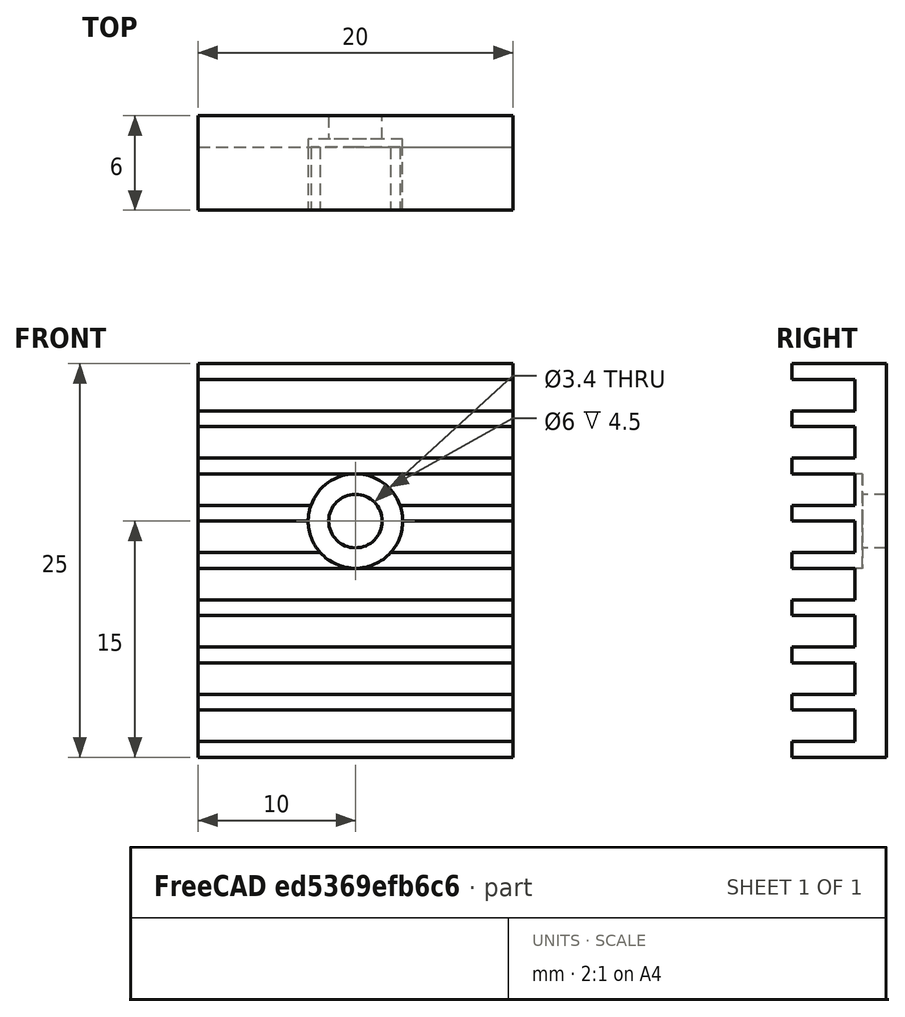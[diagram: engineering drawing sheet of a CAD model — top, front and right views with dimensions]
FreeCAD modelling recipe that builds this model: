
FCSTD DOCUMENT  (FreeCAD 0.19R24291 (Git))
Label: HVPS_Enclosure
License: All rights reserved
LicenseURL: http://en.wikipedia.org/wiki/All_rights_reserved
objects: TechDraw::DrawViewDimension×16, Sketcher::SketchObject×4, PartDesign::Pocket×3, TechDraw::DrawViewPart×3, PartDesign::Pad×1, PartDesign::LinearPattern×1, PartDesign::Body×1, TechDraw::DrawSVGTemplate×1, TechDraw::DrawPage×1
note: 14 computed .brp shape members not serialized (recipe doc carries the construction recipe); baked Part::Feature solids carry a one-line shape summary decoded from their .brp

FEATURE [Sketcher::SketchObject] Sketch
  FullyConstrained = true
  MapMode = 5
  Placement = pos=(0,0,0) rot=(1,0,0;1.5708rad)
  Support = -> [XZ_Plane002]
  sketch-geometry (4):
    g0: LineSegment StartX=-10 StartY=12.5 StartZ=0 EndX=10 EndY=12.5 EndZ=0
    g1: LineSegment StartX=10 StartY=12.5 StartZ=0 EndX=10 EndY=-12.5 EndZ=0
    g2: LineSegment StartX=10 StartY=-12.5 StartZ=0 EndX=-10 EndY=-12.5 EndZ=0
    g3: LineSegment StartX=-10 StartY=-12.5 StartZ=0 EndX=-10 EndY=12.5 EndZ=0
  constraints (10):
    c: Coincident(g0,g1)
    c: Coincident(g1,g2)
    c: Coincident(g2,g3)
    c: Coincident(g3,g0)
    c: Horizontal(g2)
    c: Vertical(g3)
    c: Symmetric(g0,g1,g-1)
    c: Symmetric(g0,g0,g-2)
    c: DistanceY(g3,g3) = 25
    c: DistanceX(g2,g2) = 20
FEATURE [PartDesign::Pad] Pad
  Direction = (1,1,1)
  Length = 6
  Length2 = 100
  Placement = pos=(0,0,0) rot=(1,0,0;1.5708rad)
  Profile = -> Sketch
  Type = 0
FEATURE [Sketcher::SketchObject] Sketch001
  ExternalGeometry = -> [Pad]
  FullyConstrained = true
  MapMode = 5
  Placement = pos=(0,-6,2.7e-15) rot=(1,0,0;1.5708rad)
  Support = -> [Pad]
  sketch-geometry (1):
    g0: Circle CenterX=0 CenterY=2.5 CenterZ=0 NormalX=0 NormalY=0 NormalZ=1 AngleXU=0 Radius=1.7
  constraints (3):
    c: PointOnObject(g0,g-2)
    c: Diameter(g0) = 3.4
    c: DistanceY(g0,g-3) = 10
FEATURE [PartDesign::Pocket] Pocket
  BaseFeature = -> Pad
  Length = 10
  Length2 = 100
  Placement = pos=(0,0,0) rot=(1,0,0;1.5708rad)
  Profile = -> Sketch001
  Type = 0
FEATURE [Sketcher::SketchObject] Sketch002
  ExternalGeometry = -> [Pocket]
  FullyConstrained = true
  MapMode = 5
  Placement = pos=(-10,0,0) rot=(0.707107,0,-0.707107;3.14159rad)
  Support = -> [Pocket]
  sketch-geometry (5):
    g0: LineSegment StartX=-11.5 StartY=6 StartZ=0 EndX=-9.5 EndY=6 EndZ=0
    g1: LineSegment StartX=-9.5 StartY=6 StartZ=0 EndX=-9.5 EndY=2 EndZ=0
    g2: LineSegment StartX=-9.5 StartY=2 StartZ=0 EndX=-11.5 EndY=2 EndZ=0
    g3: LineSegment StartX=-11.5 StartY=2 StartZ=0 EndX=-11.5 EndY=6 EndZ=0
    g4: LineSegment StartX=-9.5 StartY=6 StartZ=0 EndX=-8.5 EndY=6 EndZ=0
  constraints (15):
    c: Coincident(g0,g1)
    c: Coincident(g1,g2)
    c: Coincident(g2,g3)
    c: Coincident(g3,g0)
    c: Horizontal(g0)
    c: Horizontal(g2)
    c: Vertical(g1)
    c: Vertical(g3)
    c: PointOnObject(g0,g-3)
    c: DistanceX(g-3,g0) = 1
    c: DistanceY(g3,g3) = 4
    c: DistanceX(g2,g2) = 2
    c: Coincident(g4,g0)
    c: PointOnObject(g4,g-3)
    c: DistanceX(g4,g4) = 1
FEATURE [PartDesign::Pocket] Pocket001
  BaseFeature = -> Pocket
  Length = 25
  Length2 = 100
  Placement = pos=(0,0,0) rot=(1,0,0;1.5708rad)
  Profile = -> Sketch002
  Type = 0
FEATURE [PartDesign::LinearPattern] LinearPattern
  BaseFeature = -> Pocket001
  Direction = -> Z_Axis002
  Length = 21
  Occurrences = 8
  Originals = -> [Pocket001]
  Placement = pos=(0,0,0) rot=(1,0,0;1.5708rad)
  Reversed = true
FEATURE [Sketcher::SketchObject] Sketch003
  ExternalGeometry = -> [LinearPattern]
  FullyConstrained = true
  MapMode = 5
  Placement = pos=(0,-6,2.7e-15) rot=(1,0,0;1.5708rad)
  Support = -> [LinearPattern]
  sketch-geometry (1):
    g0: Circle CenterX=0 CenterY=2.5 CenterZ=0 NormalX=0 NormalY=0 NormalZ=1 AngleXU=0 Radius=3
  constraints (2):
    c: Coincident(g0,g-3)
    c: Diameter(g0) = 6
FEATURE [PartDesign::Pocket] Pocket002
  BaseFeature = -> LinearPattern
  Length = 4.5
  Length2 = 100
  Placement = pos=(0,0,0) rot=(1,0,0;1.5708rad)
  Profile = -> Sketch003
  Type = 0
FEATURE [PartDesign::Body] Body002  label="Heatsink"
  Group = -> [Sketch,Pad,Sketch001,Pocket,Sketch002,Pocket001,LinearPattern,Sketch003,Pocket002]
  Origin = -> Origin002
  Placement = pos=(0,100,0) rot=(0,0,1;0rad)
  Tip = -> Pocket002
FEATURE [TechDraw::DrawViewPart] View  label="front"
  CoarseView = false
  Direction = (0,-1,0)
  Focus = 100
  HardHidden = false
  IsoCount = 0
  IsoHidden = false
  IsoVisible = false
  LockPosition = false
  Perspective = false
  Rotation = 0
  Scale = 3
  ScaleType = 2
  SeamHidden = false
  SeamVisible = true
  SmoothHidden = false
  SmoothVisible = true
  Source = -> [Body002]
  X = 220.183
  XDirection = (1,0,0)
  Y = 124.936
FEATURE [TechDraw::DrawViewPart] View001  label="side"
  CoarseView = false
  Direction = (1,0,0)
  Focus = 100
  HardHidden = false
  IsoCount = 0
  IsoHidden = false
  IsoVisible = false
  LockPosition = false
  Perspective = false
  Rotation = 0
  Scale = 3
  ScaleType = 2
  SeamHidden = false
  SeamVisible = true
  SmoothHidden = false
  SmoothVisible = true
  Source = -> [Body002]
  X = 143.974
  XDirection = (0,1,0)
  Y = 125.785
FEATURE [TechDraw::DrawViewDimension] Dimension
  Arbitrary = false
  ArbitraryTolerances = false
  EqualTolerance = true
  FormatSpec = ⌀%.2f
  FormatSpecOverTolerance = %+.2f
  FormatSpecUnderTolerance = %+.2f
  Inverted = false
  LockPosition = false
  MeasureType = 1
  OverTolerance = 0
  References2D = -> [View]
  Rotation = 0
  ScaleType = 0
  TheoreticalExact = false
  Type = 5
  UnderTolerance = 0
  X = -40.1954
  Y = -0.362121
FEATURE [TechDraw::DrawViewDimension] Dimension001
  Arbitrary = false
  ArbitraryTolerances = false
  EqualTolerance = true
  FormatSpec = ⌀%.2f
  FormatSpecOverTolerance = %+.2f
  FormatSpecUnderTolerance = %+.2f
  Inverted = false
  LockPosition = false
  MeasureType = 1
  OverTolerance = 0
  References2D = -> [View]
  Rotation = 0
  ScaleType = 0
  TheoreticalExact = false
  Type = 5
  UnderTolerance = 0
  X = 38.4341
  Y = 1.73625
FEATURE [TechDraw::DrawViewDimension] Dimension002
  Arbitrary = false
  ArbitraryTolerances = false
  EqualTolerance = true
  FormatSpec = %.2f
  FormatSpecOverTolerance = %+.2f
  FormatSpecUnderTolerance = %+.2f
  Inverted = false
  LockPosition = false
  MeasureType = 1
  OverTolerance = 0
  References2D = -> [View]
  Rotation = 0
  ScaleType = 0
  TheoreticalExact = false
  Type = 2
  UnderTolerance = 0
  X = -51.2927
  Y = 0.724242
FEATURE [TechDraw::DrawViewDimension] Dimension003
  Arbitrary = false
  ArbitraryTolerances = false
  EqualTolerance = true
  FormatSpec = %.2f
  FormatSpecOverTolerance = %+.2f
  FormatSpecUnderTolerance = %+.2f
  Inverted = false
  LockPosition = false
  MeasureType = 1
  OverTolerance = 0
  References2D = -> [View]
  Rotation = 0
  ScaleType = 0
  TheoreticalExact = false
  Type = 1
  UnderTolerance = 0
  X = -0.289697
  Y = 52.8539
FEATURE [TechDraw::DrawViewDimension] Dimension004
  Arbitrary = false
  ArbitraryTolerances = false
  EqualTolerance = true
  FormatSpec = %.2f
  FormatSpecOverTolerance = %+.2f
  FormatSpecUnderTolerance = %+.2f
  Inverted = false
  LockPosition = false
  MeasureType = 1
  OverTolerance = 0
  References2D = -> [View]
  Rotation = 0
  ScaleType = 0
  TheoreticalExact = false
  Type = 2
  UnderTolerance = 0
  X = 39.7925
  Y = 49.9863
FEATURE [TechDraw::DrawViewDimension] Dimension005
  Arbitrary = false
  ArbitraryTolerances = false
  EqualTolerance = true
  FormatSpec = %.2f
  FormatSpecOverTolerance = %+.2f
  FormatSpecUnderTolerance = %+.2f
  Inverted = false
  LockPosition = false
  MeasureType = 1
  OverTolerance = 0
  References2D = -> [View]
  Rotation = 0
  ScaleType = 0
  TheoreticalExact = false
  Type = 2
  UnderTolerance = 0
  X = 48.0725
  Y = 7.28415
FEATURE [TechDraw::DrawViewDimension] Dimension006
  Arbitrary = false
  ArbitraryTolerances = false
  EqualTolerance = true
  FormatSpec = %.2f
  FormatSpecOverTolerance = %+.2f
  FormatSpecUnderTolerance = %+.2f
  Inverted = false
  LockPosition = false
  MeasureType = 1
  OverTolerance = 0
  References2D = -> [View001]
  Rotation = 0
  ScaleType = 0
  TheoreticalExact = false
  Type = 1
  UnderTolerance = 0
  X = -1.04291
  Y = 60.444
FEATURE [TechDraw::DrawViewDimension] Dimension007
  Arbitrary = false
  ArbitraryTolerances = false
  EqualTolerance = true
  FormatSpec = %.2f
  FormatSpecOverTolerance = %+.2f
  FormatSpecUnderTolerance = %+.2f
  Inverted = false
  LockPosition = false
  MeasureType = 1
  OverTolerance = 0
  References2D = -> [View001]
  Rotation = 0
  ScaleType = 0
  TheoreticalExact = false
  Type = 1
  UnderTolerance = 0
  X = -25.5963
  Y = 50.1436
FEATURE [TechDraw::DrawViewPart] View002  label="angle"
  CoarseView = false
  Direction = (-0.573,-0.798,0.188)
  Focus = 100
  HardHidden = false
  IsoCount = 0
  IsoHidden = false
  IsoVisible = false
  LockPosition = false
  Perspective = false
  Rotation = 0
  Scale = 3
  ScaleType = 2
  SeamHidden = false
  SeamVisible = true
  SmoothHidden = false
  SmoothVisible = true
  Source = -> [Body002]
  X = 69.9282
  XDirection = (0.765,-0.603,-0.226)
  Y = 84.9669
FEATURE [TechDraw::DrawViewDimension] Dimension008
  Arbitrary = false
  ArbitraryTolerances = false
  EqualTolerance = true
  FormatSpec = %.2f
  FormatSpecOverTolerance = %+.2f
  FormatSpecUnderTolerance = %+.2f
  Inverted = false
  LockPosition = false
  MeasureType = 0
  OverTolerance = 0
  References2D = -> [View002]
  References3D = -> [Body002]
  Rotation = 0
  ScaleType = 0
  TheoreticalExact = false
  Type = 0
  UnderTolerance = 0
  X = 42.4595
  Y = 38.5363
FEATURE [TechDraw::DrawViewDimension] Dimension009
  Arbitrary = false
  ArbitraryTolerances = false
  EqualTolerance = true
  FormatSpec = %.2f
  FormatSpecOverTolerance = %+.2f
  FormatSpecUnderTolerance = %+.2f
  Inverted = false
  LockPosition = false
  MeasureType = 0
  OverTolerance = 0
  References2D = -> [View002]
  References3D = -> [Body002]
  Rotation = 0
  ScaleType = 0
  TheoreticalExact = false
  Type = 0
  UnderTolerance = 0
  X = 50.3543
  Y = 2.39597
FEATURE [TechDraw::DrawViewDimension] Dimension010
  Arbitrary = false
  ArbitraryTolerances = false
  EqualTolerance = true
  FormatSpec = %.2f
  FormatSpecOverTolerance = %+.2f
  FormatSpecUnderTolerance = %+.2f
  Inverted = false
  LockPosition = false
  MeasureType = 0
  OverTolerance = 0
  References2D = -> [View002]
  References3D = -> [Body002]
  Rotation = 0
  ScaleType = 0
  TheoreticalExact = false
  Type = 0
  UnderTolerance = 0
  X = -31.6247
  Y = -24.1661
FEATURE [TechDraw::DrawViewDimension] Dimension011
  Arbitrary = false
  ArbitraryTolerances = false
  EqualTolerance = true
  FormatSpec = %.2f
  FormatSpecOverTolerance = %+.2f
  FormatSpecUnderTolerance = %+.2f
  Inverted = false
  LockPosition = false
  MeasureType = 0
  OverTolerance = 0
  References2D = -> [View002]
  References3D = -> [Body002]
  Rotation = 0
  ScaleType = 0
  TheoreticalExact = false
  Type = 0
  UnderTolerance = 0
  X = 15.3441
  Y = 70.9305
FEATURE [TechDraw::DrawViewDimension] Dimension012
  Arbitrary = false
  ArbitraryTolerances = false
  EqualTolerance = true
  FormatSpec = %.2f
  FormatSpecOverTolerance = %+.2f
  FormatSpecUnderTolerance = %+.2f
  Inverted = false
  LockPosition = false
  MeasureType = 0
  OverTolerance = 0
  References2D = -> [View002]
  References3D = -> [Body002]
  Rotation = 0
  ScaleType = 0
  TheoreticalExact = false
  Type = 0
  UnderTolerance = 0
  X = -38.801
  Y = -13.342
FEATURE [TechDraw::DrawViewDimension] Dimension013
  Arbitrary = false
  ArbitraryTolerances = false
  EqualTolerance = true
  FormatSpec = %.2f
  FormatSpecOverTolerance = %+.2f
  FormatSpecUnderTolerance = %+.2f
  Inverted = false
  LockPosition = false
  MeasureType = 0
  OverTolerance = 0
  References2D = -> [View002]
  References3D = -> [Body002]
  Rotation = 0
  ScaleType = 0
  TheoreticalExact = false
  Type = 0
  UnderTolerance = 0
  X = 20.0683
  Y = -55.0714
FEATURE [TechDraw::DrawViewDimension] Dimension014
  Arbitrary = false
  ArbitraryTolerances = false
  EqualTolerance = true
  FormatSpec = %.2f
  FormatSpecOverTolerance = %+.2f
  FormatSpecUnderTolerance = %+.2f
  Inverted = false
  LockPosition = false
  MeasureType = 1
  OverTolerance = 0
  References2D = -> [View001]
  Rotation = 0
  ScaleType = 0
  TheoreticalExact = false
  Type = 2
  UnderTolerance = 0
  X = -24.7658
  Y = 33.3088
FEATURE [TechDraw::DrawViewDimension] Dimension015
  Arbitrary = false
  ArbitraryTolerances = false
  EqualTolerance = true
  FormatSpec = %.2f
  FormatSpecOverTolerance = %+.2f
  FormatSpecUnderTolerance = %+.2f
  Inverted = false
  LockPosition = false
  MeasureType = 1
  OverTolerance = 0
  References2D = -> [View001]
  Rotation = 0
  ScaleType = 0
  TheoreticalExact = false
  Type = 2
  UnderTolerance = 0
  X = -20.0775
  Y = -4.5
FEATURE [TechDraw::DrawSVGTemplate] Template
  EditableTexts = Designed_by_Name=Corwin Hansen; FC-Date=09/09/2021; FC-Title=TO-264 Oil Heatsink
  Height = 210
  Orientation = 1
  Width = 297
FEATURE [TechDraw::DrawPage] Page  label="Heatsink_Drawing"
  KeepUpdated = true
  NextBalloonIndex = 2
  ProjectionType = 0
  Template = -> Template
  Views = -> [View,View001,Dimension,Dimension001,Dimension002,Dimension003,Dimension004,Dimension005,Dimension006,Dimension007,View002,Dimension008,Dimension009,Dimension010,Dimension011,Dimension012,Dimension013,Dimension014,Dimension015]
